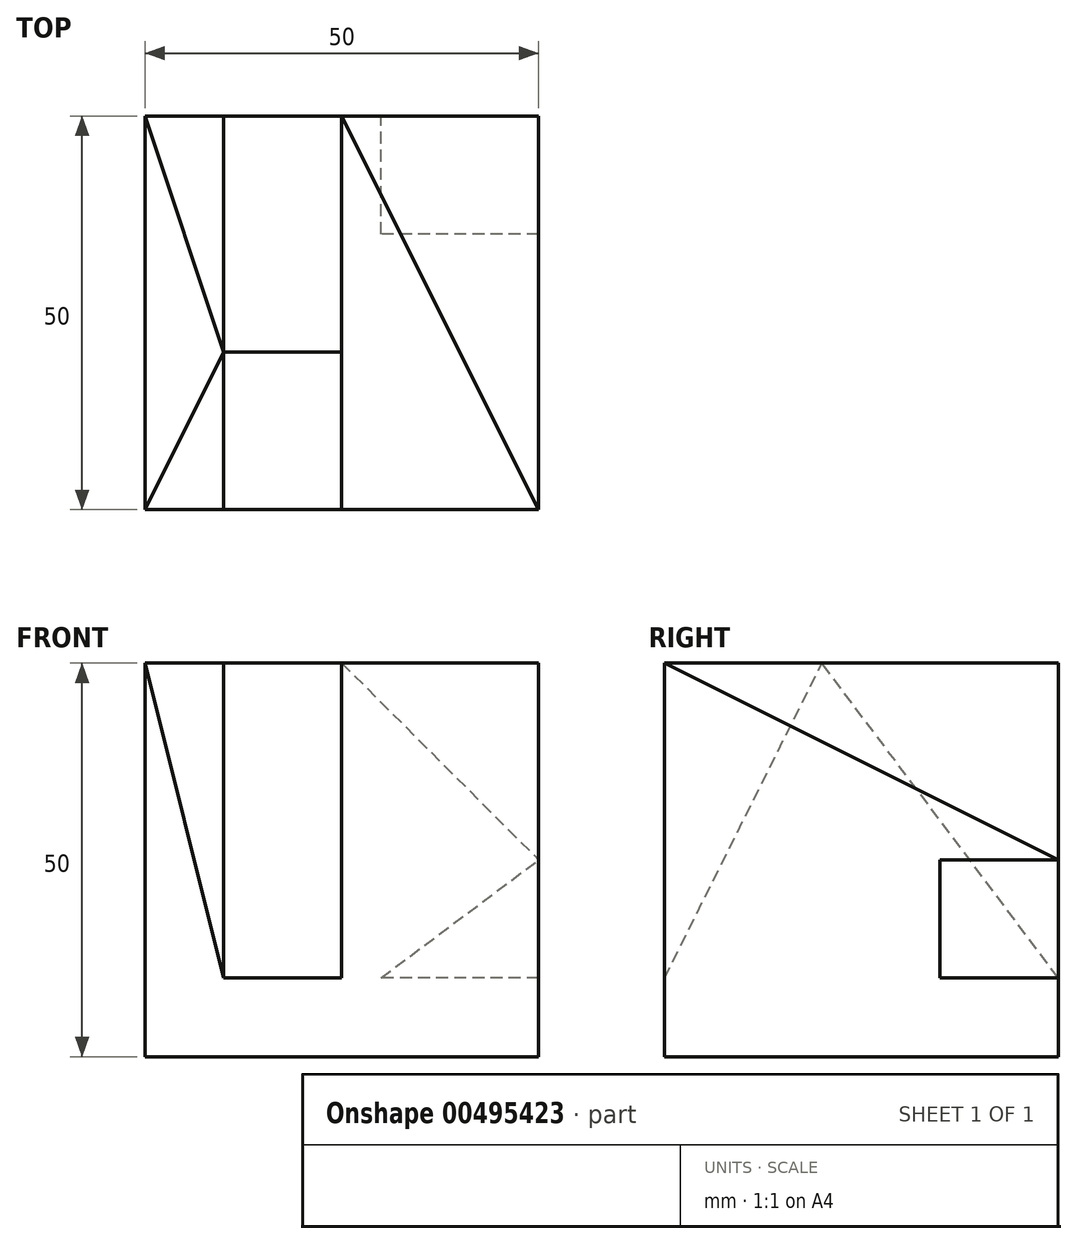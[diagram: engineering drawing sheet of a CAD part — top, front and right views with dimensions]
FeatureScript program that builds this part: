
annotation { "Feature Type Name" : "Feature", "Feature Type Description" : "" }
export const myFeature = defineFeature(function(context is Context, id is Id, definition is map)
    precondition{}
    {
        {
            var Q0;
            Q0=qCreatedBy(makeId("Top.planeOp"),FACE);
            var sketch = newSketch(context, id + "F0", { "sketchPlane" : qUnion([Q0])});
            skLineSegment(sketch, "E0.bottom", {"start": v(-25, 25) * mm, "end": v(25, 25) * mm});
            skLineSegment(sketch, "E0.top", {"start": v(-25, -25) * mm, "end": v(25, -25) * mm});
            skLineSegment(sketch, "E0.left", {"start": v(-25, 25) * mm, "end": v(-25, -25) * mm});
            skLineSegment(sketch, "E0.right", {"start": v(25, 25) * mm, "end": v(25, -25) * mm});
            skSolve(sketch);
        }
        {
            var Q0;
            Q0 = qSketchRegion(id + "F0", true);
            extrude(context, id + "F1", {"entities" : qUnion([Q0]), "depth" : 50 * mm});
        }
        {
            var Q0;
            Q0=makeQuery(id+"F1.opExtrude","CAP_FACE",FACE,{"disambiguationData":[OSD([sQuery(id+"F0.wireOp",EDGE,"E0.bottom"),sQuery(id+"F0.wireOp",EDGE,"E0.top"),sQuery(id+"F0.wireOp",EDGE,"E0.left"),sQuery(id+"F0.wireOp",EDGE,"E0.right")])],"isStart":false});
            var sketch = newSketch(context, id + "F2", { "sketchPlane" : qUnion([Q0])});
            skLineSegment(sketch, "E1", {"start": v(-25, -5) * mm, "end": v(25, -5) * mm});
            skSolve(sketch);
        }
        {
            var Q0;
            Q0=makeQuery(id+"F1.opExtrude","SWEPT_FACE",FACE,{"disambiguationData":[OSD([sQuery(id+"F0.wireOp",EDGE,"E0.top")])]});
            var sketch = newSketch(context, id + "F3", { "sketchPlane" : qUnion([Q0])});
            skLineSegment(sketch, "E2", {"start": v(-25, 10) * mm, "end": v(25, 10) * mm});
            skSolve(sketch);
        }
        {
            var Q0;
            Q0=makeQuery(id+"F1.opExtrude","SWEPT_FACE",FACE,{"disambiguationData":[OSD([sQuery(id+"F0.wireOp",EDGE,"E0.left")])]});
            var sketch = newSketch(context, id + "F4", { "sketchPlane" : qUnion([Q0])});
            skLineSegment(sketch, "E3", {"start": v(5, 50) * mm, "end": v(25, 10) * mm});
            skLineSegment(sketch, "E4", {"start": v(25, 10) * mm, "end": v(25, 50) * mm});
            skLineSegment(sketch, "E5", {"start": v(25, 50) * mm, "end": v(5, 50) * mm});
            skSolve(sketch);
        }
        {
            var Q0;
            {var subQ0=sQuery(id+"F3.wireOp",EDGE,"E2");Q0=makeQuery(id+"F3.imprint","IMPRINT",FACE,{"disambiguationData":[TD([[makeQuery(id+"F3.imprint","IMPRINT",EDGE,{"derivedFrom":subQ0}),1.0]])]});}
            var sketch = newSketch(context, id + "F5", { "sketchPlane" : qUnion([Q0])});
            skLineSegment(sketch, "E6.bottom", {"start": v(-15, 50) * mm, "end": v(0, 50) * mm});
            skLineSegment(sketch, "E6.top", {"start": v(-15, 10) * mm, "end": v(0, 10) * mm});
            skLineSegment(sketch, "E6.left", {"start": v(-15, 50) * mm, "end": v(-15, 10) * mm});
            skLineSegment(sketch, "E6.right", {"start": v(0, 50) * mm, "end": v(0, 10) * mm});
            skSolve(sketch);
        }
        {
            var Q0;
            Q0=makeQuery(id+"F5.imprint","IMPRINT",FACE,{"disambiguationData":[TD([[makeQuery(id+"F5.imprint","IMPRINT",EDGE,{"derivedFrom":sQuery(id+"F5.wireOp",EDGE,"E6.bottom")}),-1.0]])]});
            var Q1;
            Q1=sQuery(id+"F4.wireOp",EDGE,"E3");
            sweep(context, id + "F6", {"operationType" : NewBodyOperationType.REMOVE, "profiles" : qUnion([Q0]), "path" : qUnion([Q1])});
        }
        {
            var Q0;
            Q0=makeQuery(id+"F1.opExtrude","SWEPT_FACE",FACE,{"disambiguationData":[OSD([sQuery(id+"F0.wireOp",EDGE,"E0.left")])]});
            var sketch = newSketch(context, id + "F7", { "sketchPlane" : qUnion([Q0])});
            skLineSegment(sketch, "E7", {"start": v(-25, 50) * mm, "end": v(-25, 10) * mm});
            skLineSegment(sketch, "E8", {"start": v(-25, 10) * mm, "end": v(5, 50) * mm});
            skLineSegment(sketch, "E9", {"start": v(5, 50) * mm, "end": v(-25, 50) * mm});
            skSolve(sketch);
        }
        {
            var Q0;
            Q0=makeQuery(id+"F1.opExtrude","SWEPT_FACE",FACE,{"disambiguationData":[OSD([sQuery(id+"F0.wireOp",EDGE,"E0.bottom")])]});
            var sketch = newSketch(context, id + "F8", { "sketchPlane" : qUnion([Q0])});
            skLineSegment(sketch, "E10.bottom", {"start": v(0, 50) * mm, "end": v(15, 50) * mm});
            skLineSegment(sketch, "E10.top", {"start": v(0, 10) * mm, "end": v(15, 10) * mm});
            skLineSegment(sketch, "E10.left", {"start": v(0, 50) * mm, "end": v(0, 10) * mm});
            skLineSegment(sketch, "E10.right", {"start": v(15, 50) * mm, "end": v(15, 10) * mm});
            skSolve(sketch);
        }
        {
            var Q0;
            Q0=makeQuery(id+"F8.imprint","IMPRINT",FACE,{"disambiguationData":[TD([[makeQuery(id+"F8.imprint","IMPRINT",EDGE,{"derivedFrom":sQuery(id+"F8.wireOp",EDGE,"E10.bottom")}),1.0]])]});
            var Q1;
            Q1=sQuery(id+"F7.wireOp",EDGE,"E8");
            sweep(context, id + "F9", {"operationType" : NewBodyOperationType.REMOVE, "profiles" : qUnion([Q0]), "path" : qUnion([Q1])});
        }
        {
            var Q0;
            Q0=makeQuery(id+"F1.opExtrude","SWEPT_FACE",FACE,{"disambiguationData":[OSD([sQuery(id+"F0.wireOp",EDGE,"E0.bottom")])]});
            var sketch = newSketch(context, id + "F10", { "sketchPlane" : qUnion([Q0])});
            skLineSegment(sketch, "E11", {"start": v(-25, 25) * mm, "end": v(-25, 10) * mm});
            skLineSegment(sketch, "E12", {"start": v(-25, 10) * mm, "end": v(-5, 10) * mm});
            skLineSegment(sketch, "E13", {"start": v(-5, 10) * mm, "end": v(-25, 25) * mm});
            skSolve(sketch);
        }
        {
            var Q0;
            Q0 = qSketchRegion(id + "F10", true);
            extrude(context, id + "F11", {"entities" : qUnion([Q0]), "operationType" : NewBodyOperationType.REMOVE, "oppositeDirection" : true, "depth" : 15 * mm});
        }
        {
            var Q0;
            {var subQ0=sQuery(id+"F3.wireOp",EDGE,"E2");Q0=makeQuery(id+"F3.imprint","IMPRINT",FACE,{"disambiguationData":[TD([[makeQuery(id+"F3.imprint","IMPRINT",EDGE,{"derivedFrom":subQ0}),1.0]])]});}
            var sketch = newSketch(context, id + "F12", { "sketchPlane" : qUnion([Q0])});
            skLineSegment(sketch, "E14", {"start": v(-25, 50) * mm, "end": v(-15, 50) * mm});
            skLineSegment(sketch, "E15", {"start": v(-15, 50) * mm, "end": v(-15, 10) * mm});
            skLineSegment(sketch, "E16", {"start": v(-15, 10) * mm, "end": v(-25, 50) * mm});
            skSolve(sketch);
        }
        {
            var Q0;
            Q0=makeQuery(id+"F1.opExtrude","SWEPT_FACE",FACE,{"disambiguationData":[OSD([sQuery(id+"F0.wireOp",EDGE,"E0.left")])]});
            var sketch = newSketch(context, id + "F13", { "sketchPlane" : qUnion([Q0])});
            skLineSegment(sketch, "E17", {"start": v(25, 50) * mm, "end": v(5, 50) * mm});
            skLineSegment(sketch, "E18", {"start": v(5, 50) * mm, "end": v(25, 10) * mm});
            skLineSegment(sketch, "E19", {"start": v(25, 10) * mm, "end": v(25, 50) * mm});
            skSolve(sketch);
        }
        {
            var Q0;
            Q0=makeQuery(id+"F12.imprint","IMPRINT",FACE,{"disambiguationData":[TD([[makeQuery(id+"F12.imprint","IMPRINT",EDGE,{"derivedFrom":sQuery(id+"F12.wireOp",EDGE,"E14")}),-1.0]])]});
            var Q1;
            Q1=sQuery(id+"F13.wireOp",EDGE,"E18");
            sweep(context, id + "F14", {"operationType" : NewBodyOperationType.REMOVE, "profiles" : qUnion([Q0]), "path" : qUnion([Q1])});
        }
        {
            var Q0;
            Q0=makeQuery(id+"F1.opExtrude","SWEPT_FACE",FACE,{"disambiguationData":[OSD([sQuery(id+"F0.wireOp",EDGE,"E0.bottom")])]});
            var sketch = newSketch(context, id + "F15", { "sketchPlane" : qUnion([Q0])});
            skLineSegment(sketch, "E20", {"start": v(15, 50) * mm, "end": v(25, 50) * mm});
            skLineSegment(sketch, "E21", {"start": v(25, 50) * mm, "end": v(15, 10) * mm});
            skLineSegment(sketch, "E22", {"start": v(15, 10) * mm, "end": v(15, 50) * mm});
            skSolve(sketch);
        }
        {
            var Q0;
            Q0=makeQuery(id+"F15.imprint","IMPRINT",FACE,{"disambiguationData":[TD([[makeQuery(id+"F15.imprint","IMPRINT",EDGE,{"derivedFrom":sQuery(id+"F15.wireOp",EDGE,"E20")}),1.0]])]});
            var Q1;
            Q1=sQuery(id+"F7.wireOp",EDGE,"E8");
            sweep(context, id + "F16", {"operationType" : NewBodyOperationType.REMOVE, "profiles" : qUnion([Q0]), "path" : qUnion([Q1])});
        }
        {
            var Q0;
            Q0=makeQuery(id+"F1.opExtrude","SWEPT_FACE",FACE,{"disambiguationData":[OSD([sQuery(id+"F0.wireOp",EDGE,"E0.right")])]});
            var sketch = newSketch(context, id + "F17", { "sketchPlane" : qUnion([Q0])});
            skLineSegment(sketch, "E23", {"start": v(-25, 50) * mm, "end": v(25, 25) * mm});
            skLineSegment(sketch, "E24", {"start": v(25, 25) * mm, "end": v(25, 50) * mm});
            skLineSegment(sketch, "E25", {"start": v(25, 50) * mm, "end": v(-25, 50) * mm});
            skSolve(sketch);
        }
        {
            var Q0;
            Q0=makeQuery(id+"F1.opExtrude","SWEPT_FACE",FACE,{"disambiguationData":[OSD([sQuery(id+"F0.wireOp",EDGE,"E0.bottom")])]});
            var sketch = newSketch(context, id + "F18", { "sketchPlane" : qUnion([Q0])});
            skLineSegment(sketch, "E26", {"start": v(-25, 50) * mm, "end": v(0, 50) * mm});
            skLineSegment(sketch, "E27", {"start": v(0, 50) * mm, "end": v(-25, 25) * mm});
            skLineSegment(sketch, "E28", {"start": v(-25, 25) * mm, "end": v(-25, 50) * mm});
            skSolve(sketch);
        }
        {
            var Q0;
            Q0=makeQuery(id+"F18.imprint","IMPRINT",FACE,{"disambiguationData":[TD([[makeQuery(id+"F18.imprint","IMPRINT",EDGE,{"derivedFrom":sQuery(id+"F18.wireOp",EDGE,"E26")}),1.0]])]});
            var Q1;
            Q1=sQuery(id+"F17.wireOp",EDGE,"E23");
            sweep(context, id + "F19", {"operationType" : NewBodyOperationType.REMOVE, "profiles" : qUnion([Q0]), "path" : qUnion([Q1])});
        }
    });
